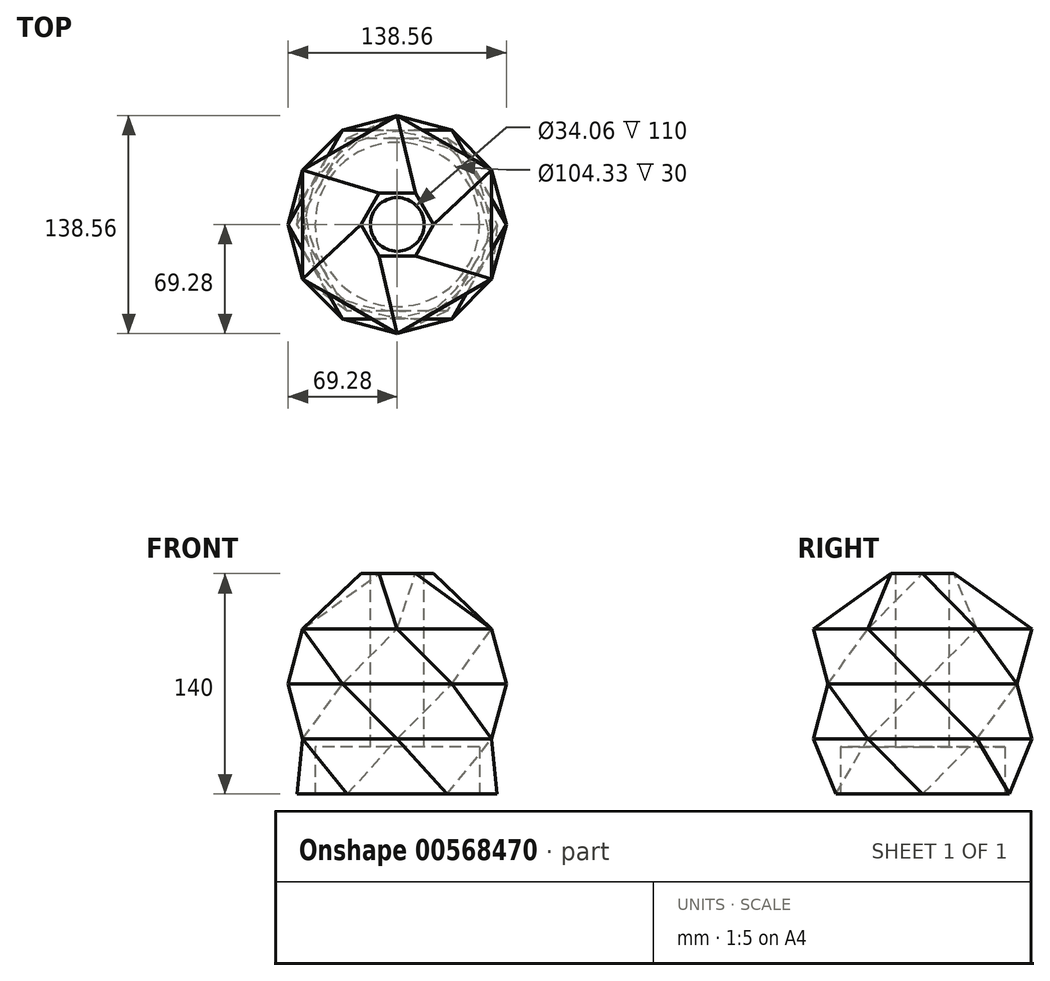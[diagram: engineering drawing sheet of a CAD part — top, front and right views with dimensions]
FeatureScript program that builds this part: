
annotation { "Feature Type Name" : "Feature", "Feature Type Description" : "" }
export const myFeature = defineFeature(function(context is Context, id is Id, definition is map)
    precondition{}
    {
        {
            var Q0;
            Q0=qCreatedBy(makeId("Top.planeOp"),FACE);
            cPlane(context, id + "F0", {"entities" : qUnion([Q0]), "cplaneType" : CPlaneType.OFFSET, "offset" : 35 * mm, "width" : 150 * mm, "height" : 150 * mm});
        }
        {
            var Q0;
            Q0=qCreatedBy(id+"F0.planeOp",FACE);
            cPlane(context, id + "F1", {"entities" : qUnion([Q0]), "cplaneType" : CPlaneType.OFFSET, "offset" : 35 * mm, "width" : 150 * mm, "height" : 150 * mm});
        }
        {
            var Q0;
            Q0=qCreatedBy(id+"F1.planeOp",FACE);
            cPlane(context, id + "F2", {"entities" : qUnion([Q0]), "cplaneType" : CPlaneType.OFFSET, "offset" : 35 * mm, "width" : 150 * mm, "height" : 150 * mm});
        }
        {
            var Q0;
            Q0=qCreatedBy(id+"F2.planeOp",FACE);
            cPlane(context, id + "F3", {"entities" : qUnion([Q0]), "cplaneType" : CPlaneType.OFFSET, "offset" : 35 * mm, "width" : 150 * mm, "height" : 150 * mm});
        }
        {
            var Q0;
            Q0=qCreatedBy(makeId("Top.planeOp"),FACE);
            var sketch = newSketch(context, id + "F4", { "sketchPlane" : qUnion([Q0])});
            skCircle(sketch, "E0.cCircle", {"center": v(0, 0) * mm, "radius": 55 * mm, "construction": true});
            skLineSegment(sketch, "E0.0", {"start": v(31.75, -55) * mm, "end": v(-31.75, -55) * mm});
            skLineSegment(sketch, "E0.1", {"start": v(-31.75, -55) * mm, "end": v(-63.5, 0) * mm});
            skLineSegment(sketch, "E0.2", {"start": v(-63.5, 0) * mm, "end": v(-31.75, 55) * mm});
            skLineSegment(sketch, "E0.3", {"start": v(-31.75, 55) * mm, "end": v(31.75, 55) * mm});
            skLineSegment(sketch, "E0.4", {"start": v(31.75, 55) * mm, "end": v(63.5, 0) * mm});
            skLineSegment(sketch, "E0.5", {"start": v(63.5, 0) * mm, "end": v(31.75, -55) * mm});
            skPoint(sketch, "E0.0.midPoint", {"position": v(0, -55) * mm});
            skSolve(sketch);
        }
        {
            var Q0;
            Q0=qCreatedBy(id+"F0.planeOp",FACE);
            var sketch = newSketch(context, id + "F5", { "sketchPlane" : qUnion([Q0])});
            skCircle(sketch, "E1.cCircle", {"center": v(0, 0) * mm, "radius": 60 * mm, "construction": true});
            skLineSegment(sketch, "E1.0", {"start": v(60, 34.64) * mm, "end": v(60, -34.64) * mm});
            skLineSegment(sketch, "E1.1", {"start": v(60, -34.64) * mm, "end": v(0, -69.28) * mm});
            skLineSegment(sketch, "E1.2", {"start": v(0, -69.28) * mm, "end": v(-60, -34.64) * mm});
            skLineSegment(sketch, "E1.3", {"start": v(-60, -34.64) * mm, "end": v(-60, 34.64) * mm});
            skLineSegment(sketch, "E1.4", {"start": v(-60, 34.64) * mm, "end": v(0, 69.28) * mm});
            skLineSegment(sketch, "E1.5", {"start": v(0, 69.28) * mm, "end": v(60, 34.64) * mm});
            skPoint(sketch, "E1.0.midPoint", {"position": v(60, 0) * mm});
            skSolve(sketch);
        }
        {
            var Q0;
            Q0=qCreatedBy(id+"F1.planeOp",FACE);
            var sketch = newSketch(context, id + "F6", { "sketchPlane" : qUnion([Q0])});
            skCircle(sketch, "E2.cCircle", {"center": v(0, 0) * mm, "radius": 60 * mm, "construction": true});
            skLineSegment(sketch, "E2.0", {"start": v(69.28, 0) * mm, "end": v(34.64, -60) * mm});
            skLineSegment(sketch, "E2.1", {"start": v(34.64, -60) * mm, "end": v(-34.64, -60) * mm});
            skLineSegment(sketch, "E2.2", {"start": v(-34.64, -60) * mm, "end": v(-69.28, 0) * mm});
            skLineSegment(sketch, "E2.3", {"start": v(-69.28, 0) * mm, "end": v(-34.64, 60) * mm});
            skLineSegment(sketch, "E2.4", {"start": v(-34.64, 60) * mm, "end": v(34.64, 60) * mm});
            skLineSegment(sketch, "E2.5", {"start": v(34.64, 60) * mm, "end": v(69.28, 0) * mm});
            skPoint(sketch, "E2.0.midPoint", {"position": v(51.96, -30) * mm});
            skSolve(sketch);
        }
        {
            var Q0;
            Q0=qCreatedBy(id+"F2.planeOp",FACE);
            var sketch = newSketch(context, id + "F7", { "sketchPlane" : qUnion([Q0])});
            skCircle(sketch, "E3.cCircle", {"center": v(0, 0) * mm, "radius": 60 * mm, "construction": true});
            skLineSegment(sketch, "E3.0", {"start": v(60, -34.64) * mm, "end": v(0, -69.28) * mm});
            skLineSegment(sketch, "E3.1", {"start": v(0, -69.28) * mm, "end": v(-60, -34.64) * mm});
            skLineSegment(sketch, "E3.2", {"start": v(-60, -34.64) * mm, "end": v(-60, 34.64) * mm});
            skLineSegment(sketch, "E3.3", {"start": v(-60, 34.64) * mm, "end": v(0, 69.28) * mm});
            skLineSegment(sketch, "E3.4", {"start": v(0, 69.28) * mm, "end": v(60, 34.64) * mm});
            skLineSegment(sketch, "E3.5", {"start": v(60, 34.64) * mm, "end": v(60, -34.64) * mm});
            skPoint(sketch, "E3.0.midPoint", {"position": v(30, -51.96) * mm});
            skSolve(sketch);
        }
        {
            var Q0;
            Q0=qCreatedBy(id+"F3.planeOp",FACE);
            var sketch = newSketch(context, id + "F8", { "sketchPlane" : qUnion([Q0])});
            skCircle(sketch, "E4.cCircle", {"center": v(0, 0) * mm, "radius": 20 * mm, "construction": true});
            skLineSegment(sketch, "E4.0", {"start": v(23.1, 0) * mm, "end": v(11.55, -20) * mm});
            skLineSegment(sketch, "E4.1", {"start": v(11.55, -20) * mm, "end": v(-11.55, -20) * mm});
            skLineSegment(sketch, "E4.2", {"start": v(-11.55, -20) * mm, "end": v(-23.1, 0) * mm});
            skLineSegment(sketch, "E4.3", {"start": v(-23.1, 0) * mm, "end": v(-11.55, 20) * mm});
            skLineSegment(sketch, "E4.4", {"start": v(-11.55, 20) * mm, "end": v(11.55, 20) * mm});
            skLineSegment(sketch, "E4.5", {"start": v(11.55, 20) * mm, "end": v(23.1, 0) * mm});
            skPoint(sketch, "E4.0.midPoint", {"position": v(17.32, -10) * mm});
            skSolve(sketch);
        }
        {
            var Q0;
            Q0=makeQuery(id+"F4.imprint","IMPRINT",FACE,{"disambiguationData":[TD([[makeQuery(id+"F4.imprint","IMPRINT",EDGE,{"derivedFrom":sQuery(id+"F4.wireOp",EDGE,"E0.0")}),-1.0]])]});
            var Q1;
            Q1=makeQuery(id+"F5.imprint","IMPRINT",FACE,{"disambiguationData":[TD([[makeQuery(id+"F5.imprint","IMPRINT",EDGE,{"derivedFrom":sQuery(id+"F5.wireOp",EDGE,"E1.0")}),-1.0]])]});
            var Q2;
            Q2=sQuery(id+"F4.wireOp",VERTEX,"E0.2.start");
            var Q3;
            Q3=sQuery(id+"F5.wireOp",VERTEX,"E1.4.start");
            loft(context, id + "F9", {"sheetProfilesArray" : [{ "sheetProfileEntities" : qUnion([Q0]) }, { "sheetProfileEntities" : qUnion([Q1]) }], "matchConnections" : true, "connections" : [{ "connectionEntities" : qUnion([Q2, Q3]), "connectionEdgeQueries" : qUnion([]), "connectionEdgeParameters" : [] }]});
        }
        {
            var Q1;
            Q1=qSketchRegion(id+"F5",true);
            var Q2;
            Q2=qSketchRegion(id+"F6",true);
            var Q3;
            Q3=sQuery(id+"F5.wireOp",VERTEX,"E1.3.start");
            var Q4;
            Q4=sQuery(id+"F6.wireOp",VERTEX,"E2.3.start");
            loft(context, id + "F10", {"operationType" : NewBodyOperationType.ADD, "sheetProfilesArray" : [{ "sheetProfileEntities" : qUnion([Q1]) }, { "sheetProfileEntities" : qUnion([Q2]) }], "matchConnections" : true, "connections" : [{ "connectionEntities" : qUnion([Q3, Q4]), "connectionEdgeQueries" : qUnion([]), "connectionEdgeParameters" : [] }]});
        }
        {
            var Q1;
            Q1=qSketchRegion(id+"F6",true);
            var Q2;
            Q2=qSketchRegion(id+"F7",true);
            var Q3;
            Q3=sQuery(id+"F6.wireOp",VERTEX,"E2.3.start");
            var Q4;
            Q4=sQuery(id+"F7.wireOp",VERTEX,"E3.3.start");
            loft(context, id + "F11", {"operationType" : NewBodyOperationType.ADD, "sheetProfilesArray" : [{ "sheetProfileEntities" : qUnion([Q1]) }, { "sheetProfileEntities" : qUnion([Q2]) }], "matchConnections" : true, "connections" : [{ "connectionEntities" : qUnion([Q3, Q4]), "connectionEdgeQueries" : qUnion([]), "connectionEdgeParameters" : [] }]});
        }
        {
            var Q1;
            Q1=qSketchRegion(id+"F7",true);
            var Q2;
            Q2=qSketchRegion(id+"F8",true);
            var Q3;
            Q3=sQuery(id+"F7.wireOp",VERTEX,"E3.2.start");
            var Q4;
            Q4=sQuery(id+"F8.wireOp",VERTEX,"E4.3.start");
            loft(context, id + "F12", {"operationType" : NewBodyOperationType.ADD, "sheetProfilesArray" : [{ "sheetProfileEntities" : qUnion([Q1]) }, { "sheetProfileEntities" : qUnion([Q2]) }], "matchConnections" : true, "connections" : [{ "connectionEntities" : qUnion([Q3, Q4]), "connectionEdgeQueries" : qUnion([]), "connectionEdgeParameters" : [] }]});
        }
        {
            var Q0;
            Q0=makeQuery(id+"F8.imprint","IMPRINT",FACE,{"disambiguationData":[TD([[makeQuery(id+"F8.imprint","IMPRINT",EDGE,{"derivedFrom":sQuery(id+"F8.wireOp",EDGE,"E4.0")}),-1.0]])]});
            var sketch = newSketch(context, id + "F13", { "sketchPlane" : qUnion([Q0])});
            skCircle(sketch, "E5", {"center": v(0, 0) * mm, "radius": 17.03 * mm});
            skSolve(sketch);
        }
        {
            var Q0;
            Q0 = qSketchRegion(id + "F13", true);
            extrude(context, id + "F14", {"entities" : qUnion([Q0]), "operationType" : NewBodyOperationType.REMOVE, "endBound" : BoundingType.THROUGH_ALL, "oppositeDirection" : true, "depth" : 25 * mm, "offsetDistance" : 25 * mm});
        }
        {
            var Q0;
            Q0=makeQuery(id+"F4.imprint","IMPRINT",FACE,{"disambiguationData":[TD([[makeQuery(id+"F4.imprint","IMPRINT",EDGE,{"derivedFrom":sQuery(id+"F4.wireOp",EDGE,"E0.0")}),-1.0]])]});
            var sketch = newSketch(context, id + "F15", { "sketchPlane" : qUnion([Q0])});
            skCircle(sketch, "E6", {"center": v(0, 0) * mm, "radius": 52.16 * mm});
            skSolve(sketch);
        }
        {
            var Q0;
            Q0 = qSketchRegion(id + "F15", true);
            extrude(context, id + "F16", {"entities" : qUnion([Q0]), "operationType" : NewBodyOperationType.REMOVE, "depth" : 30 * mm, "offsetDistance" : 25 * mm});
        }
    });
